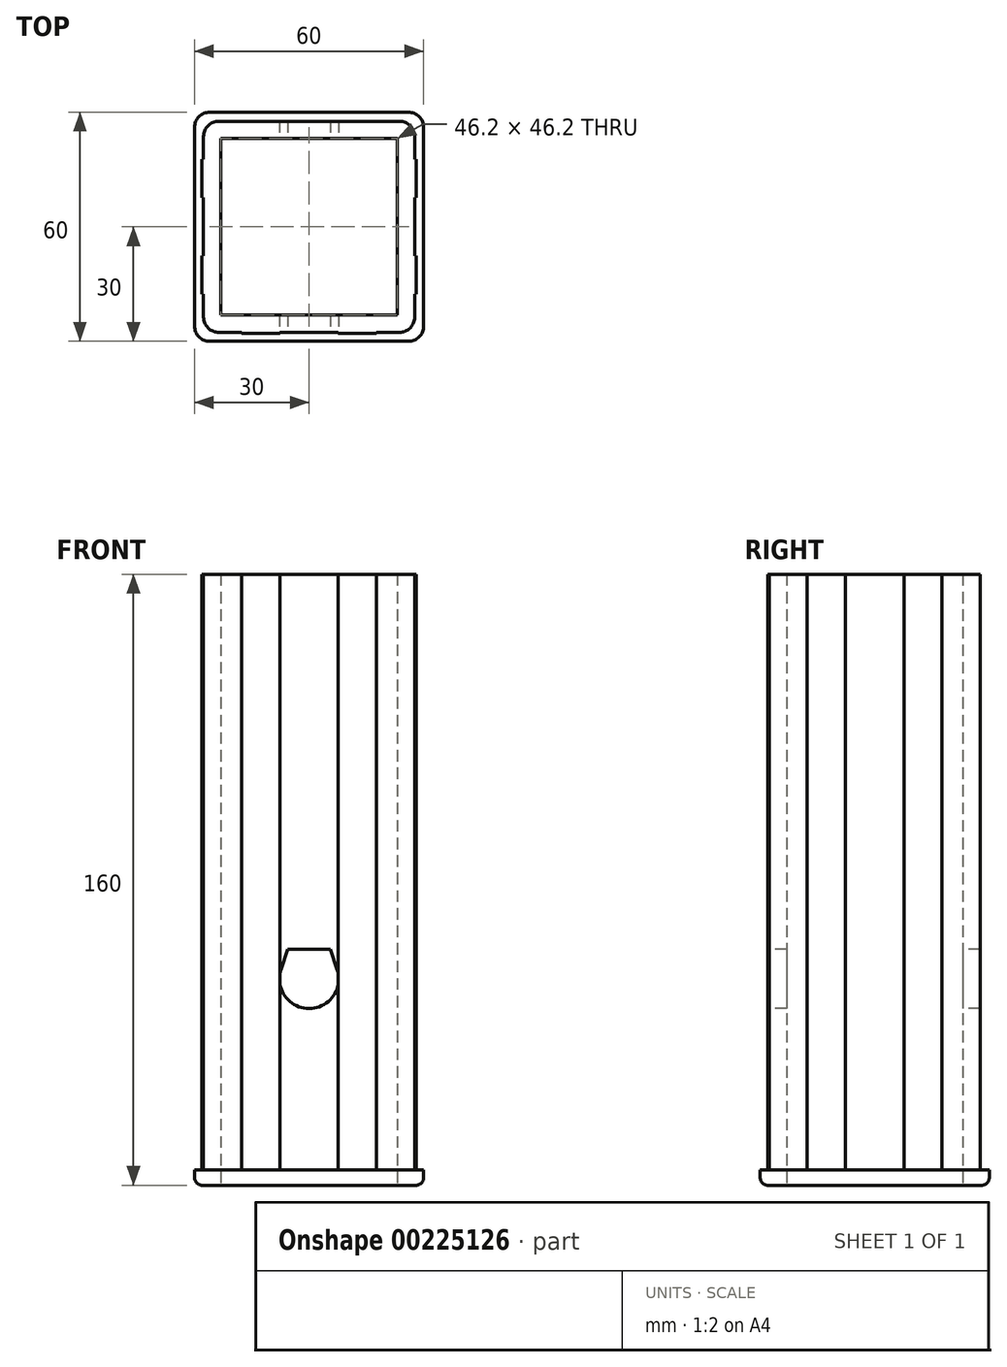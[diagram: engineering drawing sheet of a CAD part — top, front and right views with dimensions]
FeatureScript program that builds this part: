
annotation { "Feature Type Name" : "Feature", "Feature Type Description" : "" }
export const myFeature = defineFeature(function(context is Context, id is Id, definition is map)
    precondition{}
    {
        {
            var Q0;
            Q0=qCreatedBy(makeId("Top.planeOp"),FACE);
            var sketch = newSketch(context, id + "F0", { "sketchPlane" : qUnion([Q0])});
            skLineSegment(sketch, "E0.bottom", {"start": v(30, 30) * mm, "end": v(-30, 30) * mm});
            skLineSegment(sketch, "E0.top", {"start": v(30, -30) * mm, "end": v(-30, -30) * mm});
            skLineSegment(sketch, "E0.left", {"start": v(30, 30) * mm, "end": v(30, -30) * mm});
            skLineSegment(sketch, "E0.right", {"start": v(-30, 30) * mm, "end": v(-30, -30) * mm});
            skPoint(sketch, "E0.middle", {"position": v(0, 0) * mm});
            skLineSegment(sketch, "E1.bottom", {"start": v(23.1, 23.1) * mm, "end": v(-23.1, 23.1) * mm});
            skLineSegment(sketch, "E1.top", {"start": v(23.1, -23.1) * mm, "end": v(-23.1, -23.1) * mm});
            skLineSegment(sketch, "E1.left", {"start": v(23.1, 23.1) * mm, "end": v(23.1, -23.1) * mm});
            skLineSegment(sketch, "E1.right", {"start": v(-23.1, 23.1) * mm, "end": v(-23.1, -23.1) * mm});
            skLineSegment(sketch, "E2.bottom", {"start": v(27.65, 27.65) * mm, "end": v(-27.65, 27.65) * mm});
            skLineSegment(sketch, "E2.top", {"start": v(27.65, -27.65) * mm, "end": v(17.65, -27.65) * mm});
            skLineSegment(sketch, "E2.left", {"start": v(27.65, 27.65) * mm, "end": v(27.65, 17.65) * mm});
            skLineSegment(sketch, "E2.right", {"start": v(-27.65, 27.65) * mm, "end": v(-27.65, 17.65) * mm});
            skLineSegment(sketch, "E3", {"start": v(27.65, 17.65) * mm, "end": v(28.05, 17.65) * mm});
            skLineSegment(sketch, "E4", {"start": v(28.05, 17.65) * mm, "end": v(28.05, 7.65) * mm});
            skLineSegment(sketch, "E5", {"start": v(27.65, 7.65) * mm, "end": v(28.05, 7.65) * mm});
            skLineSegment(sketch, "E6.trimOffspring", {"start": v(27.65, 7.65) * mm, "end": v(27.65, -7.65) * mm});
            skLineSegment(sketch, "E7", {"start": v(27.65, -17.65) * mm, "end": v(28.05, -17.65) * mm});
            skLineSegment(sketch, "E8", {"start": v(28.05, -17.65) * mm, "end": v(28.05, -7.65) * mm});
            skLineSegment(sketch, "E9", {"start": v(28.05, -7.65) * mm, "end": v(27.65, -7.65) * mm});
            skLineSegment(sketch, "E10.trimOffspring", {"start": v(27.65, -17.65) * mm, "end": v(27.65, -27.65) * mm});
            skLineSegment(sketch, "E11", {"start": v(17.65, -27.65) * mm, "end": v(17.65, -27.95) * mm});
            skLineSegment(sketch, "E12", {"start": v(17.65, -27.95) * mm, "end": v(7.65, -27.95) * mm});
            skLineSegment(sketch, "E13", {"start": v(7.65, -27.95) * mm, "end": v(7.65, -27.65) * mm});
            skLineSegment(sketch, "E14", {"start": v(-7.65, -27.65) * mm, "end": v(-7.65, -27.95) * mm});
            skLineSegment(sketch, "E15", {"start": v(-7.65, -27.95) * mm, "end": v(-17.65, -27.95) * mm});
            skLineSegment(sketch, "E16", {"start": v(-17.65, -27.95) * mm, "end": v(-17.65, -27.65) * mm});
            skLineSegment(sketch, "E17", {"start": v(-27.65, -17.65) * mm, "end": v(-28.05, -17.65) * mm});
            skLineSegment(sketch, "E18", {"start": v(-28.05, -17.65) * mm, "end": v(-28.05, -7.65) * mm});
            skLineSegment(sketch, "E19", {"start": v(-28.05, -7.65) * mm, "end": v(-27.65, -7.65) * mm});
            skLineSegment(sketch, "E20", {"start": v(-27.65, 17.65) * mm, "end": v(-28.05, 17.65) * mm});
            skLineSegment(sketch, "E21", {"start": v(-28.05, 17.65) * mm, "end": v(-28.05, 7.65) * mm});
            skLineSegment(sketch, "E22", {"start": v(-28.05, 7.65) * mm, "end": v(-27.65, 7.65) * mm});
            skLineSegment(sketch, "E23.trimOffspring", {"start": v(-27.65, 7.65) * mm, "end": v(-27.65, -7.65) * mm});
            skLineSegment(sketch, "E24.trimOffspring", {"start": v(-27.65, -17.65) * mm, "end": v(-27.65, -27.65) * mm});
            skLineSegment(sketch, "E25.trimOffspring", {"start": v(-17.65, -27.65) * mm, "end": v(-27.65, -27.65) * mm});
            skLineSegment(sketch, "E26.trimOffspring", {"start": v(7.65, -27.65) * mm, "end": v(-7.65, -27.65) * mm});
            skSolve(sketch);
        }
        {
            var Q0;
            Q0=makeQuery(id+"F0.imprint","IMPRINT",FACE,{"disambiguationData":[TD([[makeQuery(id+"F0.imprint","IMPRINT",EDGE,{"derivedFrom":sQuery(id+"F0.wireOp",EDGE,"E1.bottom")}),-1.0]])]});
            extrude(context, id + "F1", {"entities" : qUnion([Q0]), "depth" : 156 * mm});
        }
        {
            var Q0;
            Q0=makeQuery(id+"F0.imprint","IMPRINT",FACE,{"disambiguationData":[TD([[makeQuery(id+"F0.imprint","IMPRINT",EDGE,{"derivedFrom":sQuery(id+"F0.wireOp",EDGE,"E0.bottom")}),1.0]])]});
            var Q1;
            Q1=makeQuery(id+"F0.imprint","IMPRINT",FACE,{"disambiguationData":[TD([[makeQuery(id+"F0.imprint","IMPRINT",EDGE,{"derivedFrom":sQuery(id+"F0.wireOp",EDGE,"E1.bottom")}),-1.0]])]});
            extrude(context, id + "F2", {"entities" : qUnion([Q0, Q1]), "operationType" : NewBodyOperationType.ADD, "oppositeDirection" : true, "depth" : 4 * mm});
        }
        {
            var Q0;
            Q0=makeQuery(id+"F1.opExtrude","SWEPT_EDGE",EDGE,{"disambiguationData":[OSD([sQuery(id+"F0.wireOp",EDGE,"E2.bottom"),sQuery(id+"F0.wireOp",EDGE,"E2.right")])]});
            var Q1;
            Q1=makeQuery(id+"F1.opExtrude","SWEPT_EDGE",EDGE,{"disambiguationData":[OSD([sQuery(id+"F0.wireOp",EDGE,"E24.trimOffspring"),sQuery(id+"F0.wireOp",EDGE,"E25.trimOffspring")])]});
            var Q2;
            Q2=makeQuery(id+"F1.opExtrude","SWEPT_EDGE",EDGE,{"disambiguationData":[OSD([sQuery(id+"F0.wireOp",EDGE,"E2.top"),sQuery(id+"F0.wireOp",EDGE,"E10.trimOffspring")])]});
            var Q3;
            Q3=makeQuery(id+"F1.opExtrude","SWEPT_EDGE",EDGE,{"disambiguationData":[OSD([sQuery(id+"F0.wireOp",EDGE,"E2.bottom"),sQuery(id+"F0.wireOp",EDGE,"E2.left")])]});
            var Q4;
            Q4=makeQuery(id+"F2.opExtrude","SWEPT_EDGE",EDGE,{"disambiguationData":[OSD([sQuery(id+"F0.wireOp",EDGE,"E0.bottom"),sQuery(id+"F0.wireOp",EDGE,"E0.left")])]});
            var Q5;
            Q5=makeQuery(id+"F2.opExtrude","SWEPT_EDGE",EDGE,{"disambiguationData":[OSD([sQuery(id+"F0.wireOp",EDGE,"E0.top"),sQuery(id+"F0.wireOp",EDGE,"E0.left")])]});
            var Q6;
            Q6=makeQuery(id+"F2.opExtrude","SWEPT_EDGE",EDGE,{"disambiguationData":[OSD([sQuery(id+"F0.wireOp",EDGE,"E0.bottom"),sQuery(id+"F0.wireOp",EDGE,"E0.right")])]});
            var Q7;
            Q7=makeQuery(id+"F2.opExtrude","SWEPT_EDGE",EDGE,{"disambiguationData":[OSD([sQuery(id+"F0.wireOp",EDGE,"E0.top"),sQuery(id+"F0.wireOp",EDGE,"E0.right")])]});
            fillet(context, id + "F3", {"entities" : qUnion([Q0, Q1, Q2, Q3, Q4, Q5, Q6, Q7]), "radius" : 4 * mm, "tangentPropagation" : true, "allowEdgeOverflow" : false});
        }
        {
            var Q0;
            Q0=makeQuery(id+"F2.opExtrude","CAP_EDGE",EDGE,{"disambiguationData":[OSD([sQuery(id+"F0.wireOp",EDGE,"E0.left")])],"isStart":false});
            fillet(context, id + "F4", {"entities" : qUnion([Q0]), "radius" : 2 * mm, "tangentPropagation" : true, "allowEdgeOverflow" : false});
        }
        {
            var Q0;
            Q0=qCreatedBy(makeId("Front.planeOp"),FACE);
            cPlane(context, id + "F5", {"entities" : qUnion([Q0]), "cplaneType" : CPlaneType.OFFSET, "offset" : 27.65 * mm, "width" : 150 * mm, "height" : 150 * mm});
        }
        {
            var Q0;
            Q0=qCreatedBy(id+"F5.planeOp",FACE);
            var sketch = newSketch(context, id + "F6", { "sketchPlane" : qUnion([Q0])});
            skArc(sketch, "E27", {"start": v(-7.37, 52.4) * mm, "mid": v(0, 42.25) * mm, "end": v(7.37, 52.4) * mm});
            skArc(sketch, "E28.cCircle", {"start": v(-7.37, 52.4) * mm, "mid": v(0, 42.25) * mm, "end": v(7.37, 52.4) * mm, "construction": true});
            skLineSegment(sketch, "E28.0", {"start": v(-5.63, 57.75) * mm, "end": v(5.63, 57.75) * mm});
            skLineSegment(sketch, "E28.1", {"start": v(5.63, 57.75) * mm, "end": v(7.37, 52.4) * mm});
            skLineSegment(sketch, "E28.4", {"start": v(-7.37, 52.4) * mm, "end": v(-5.63, 57.75) * mm});
            skPoint(sketch, "E28.0.midPoint", {"position": v(0, 57.75) * mm});
            skPoint(sketch, "E29.orphan", {"position": v(9.11, 47.04) * mm});
            skPoint(sketch, "E30.orphan", {"position": v(0, 40.42) * mm});
            skPoint(sketch, "E31.orphan", {"position": v(-9.11, 47.04) * mm});
            skSolve(sketch);
        }
        {
            var Q0;
            Q0=makeQuery(id+"F6.imprint","IMPRINT",FACE,{"disambiguationData":[TD([[makeQuery(id+"F6.imprint","IMPRINT",EDGE,{"derivedFrom":sQuery(id+"F6.wireOp",EDGE,"E27")}),1.0]])]});
            extrude(context, id + "F7", {"entities" : qUnion([Q0]), "operationType" : NewBodyOperationType.REMOVE, "oppositeDirection" : true, "depth" : 80 * mm});
        }
    });
